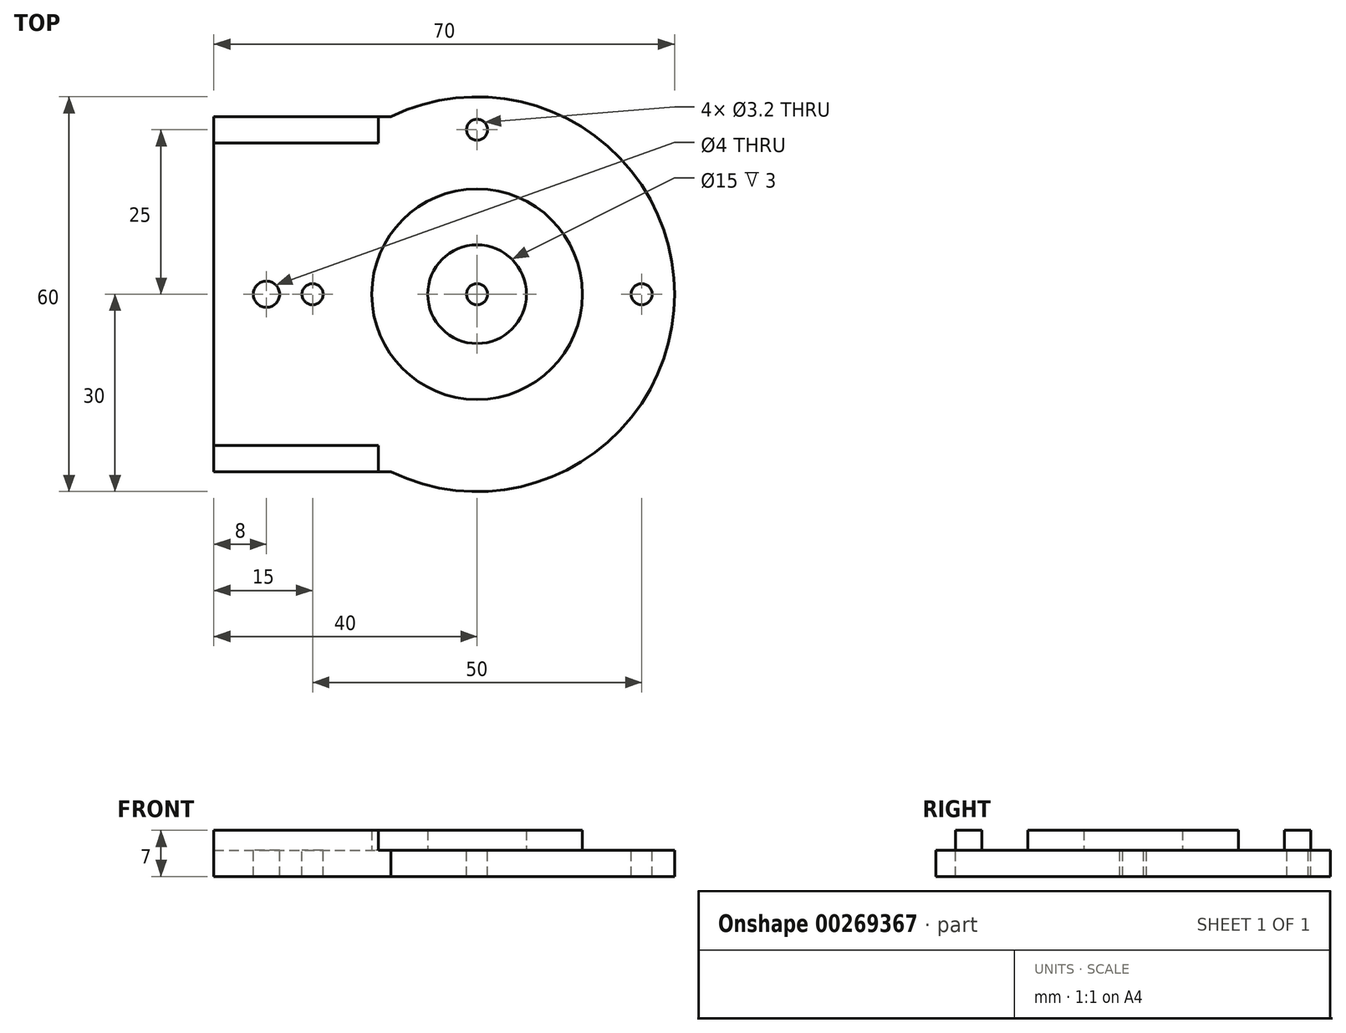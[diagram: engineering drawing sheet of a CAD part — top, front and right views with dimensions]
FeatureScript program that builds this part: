
annotation { "Feature Type Name" : "Feature", "Feature Type Description" : "" }
export const myFeature = defineFeature(function(context is Context, id is Id, definition is map)
    precondition{}
    {
        {
            var Q0;
            Q0=qCreatedBy(makeId("Top.planeOp"),FACE);
            var sketch = newSketch(context, id + "F0", { "sketchPlane" : qUnion([Q0])});
            skCircle(sketch, "E0", {"center": v(0, 0) * mm, "radius": 1.6 * mm});
            skCircle(sketch, "E1", {"center": v(0, 0) * mm, "radius": 30 * mm});
            skLineSegment(sketch, "E2", {"start": v(0, 0) * mm, "end": v(0, 25) * mm});
            skCircle(sketch, "E3", {"center": v(0, 25) * mm, "radius": 1.6 * mm});
            skCircle(sketch, "E4.1.0", {"center": v(-25, 0) * mm, "radius": 1.6 * mm});
            skCircle(sketch, "E4.3.0", {"center": v(25, 0) * mm, "radius": 1.6 * mm});
            skLineSegment(sketch, "E5.bottom", {"start": v(0, -27) * mm, "end": v(-40, -27) * mm});
            skLineSegment(sketch, "E5.top", {"start": v(0, 27) * mm, "end": v(-40, 27) * mm});
            skLineSegment(sketch, "E5.left", {"start": v(0, -27) * mm, "end": v(0, 27) * mm});
            skLineSegment(sketch, "E5.right", {"start": v(-40, -27) * mm, "end": v(-40, 27) * mm});
            skPoint(sketch, "E5.middle", {"position": v(-20, 0) * mm});
            skLineSegment(sketch, "E6", {"start": v(-40, 0) * mm, "end": v(-32, 0) * mm});
            skPoint(sketch, "E6.endSnap0", {"position": v(-40, 0) * mm});
            skCircle(sketch, "E7", {"center": v(-32, 0) * mm, "radius": 2 * mm});
            skSolve(sketch);
        }
        {
            var Q0;
            Q0 = qSketchRegion(id + "F0", true);
            extrude(context, id + "F1", {"entities" : qUnion([Q0]), "oppositeDirection" : true, "depth" : 4 * mm});
        }
        {
            var Q0;
            Q0=qCreatedBy(makeId("Top.planeOp"),FACE);
            var sketch = newSketch(context, id + "F2", { "sketchPlane" : qUnion([Q0])});
            skCircle(sketch, "E8", {"center": v(0, 0) * mm, "radius": 7.5 * mm});
            skCircle(sketch, "E9", {"center": v(0, 0) * mm, "radius": 16 * mm});
            skLineSegment(sketch, "E10.bottom", {"start": v(-40, -27) * mm, "end": v(-15, -27) * mm});
            skLineSegment(sketch, "E10.top", {"start": v(-40, -23) * mm, "end": v(-15, -23) * mm});
            skLineSegment(sketch, "E10.left", {"start": v(-40, -27) * mm, "end": v(-40, -23) * mm});
            skLineSegment(sketch, "E10.right", {"start": v(-15, -27) * mm, "end": v(-15, -23) * mm});
            skLineSegment(sketch, "E11.bottom", {"start": v(-40, 27) * mm, "end": v(-15, 27) * mm});
            skLineSegment(sketch, "E11.top", {"start": v(-40, 23) * mm, "end": v(-15, 23) * mm});
            skLineSegment(sketch, "E11.left", {"start": v(-40, 27) * mm, "end": v(-40, 23) * mm});
            skLineSegment(sketch, "E11.right", {"start": v(-15, 27) * mm, "end": v(-15, 23) * mm});
            skSolve(sketch);
        }
        {
            var Q0;
            Q0 = qSketchRegion(id + "F2", true);
            extrude(context, id + "F3", {"entities" : qUnion([Q0]), "operationType" : NewBodyOperationType.ADD, "depth" : 3 * mm});
        }
    });
